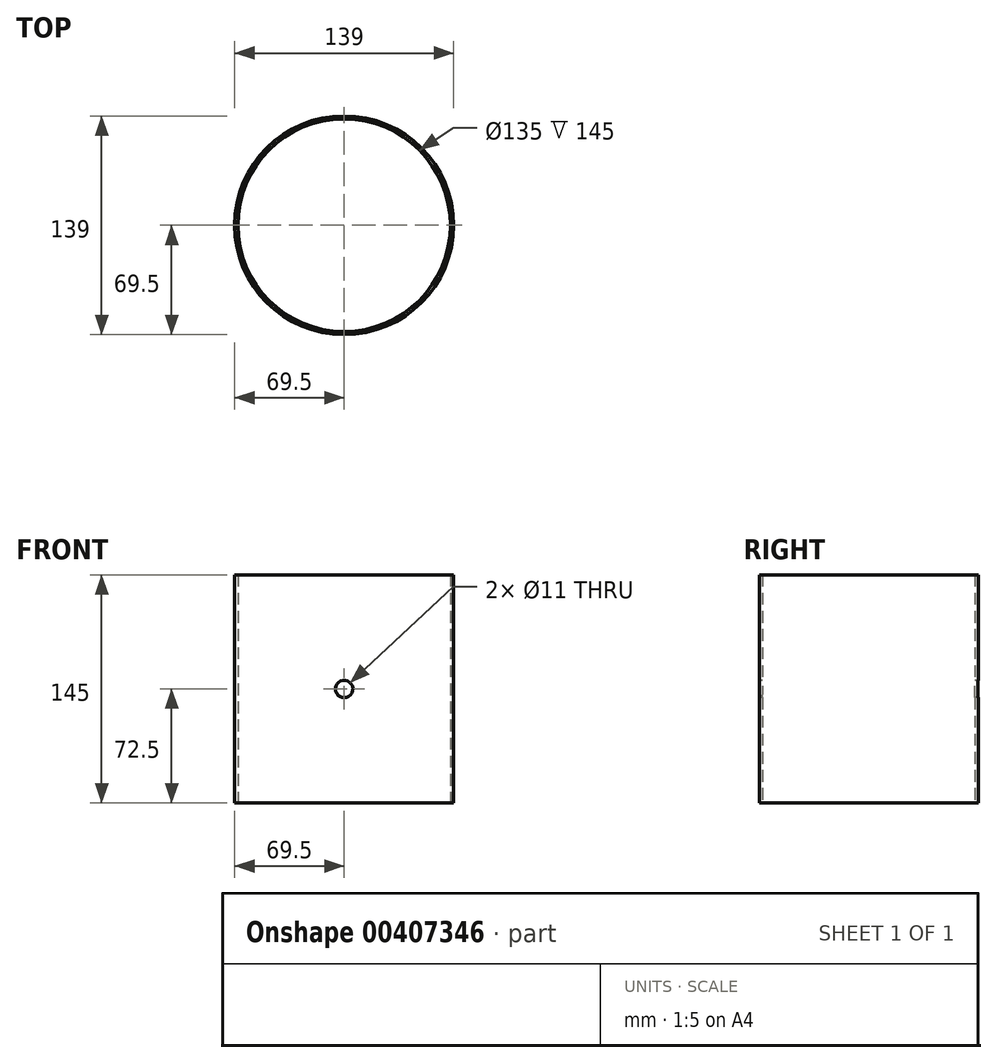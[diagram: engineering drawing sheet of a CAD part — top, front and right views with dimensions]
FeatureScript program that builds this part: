
annotation { "Feature Type Name" : "Feature", "Feature Type Description" : "" }
export const myFeature = defineFeature(function(context is Context, id is Id, definition is map)
    precondition{}
    {
        {
            var Q0;
            Q0=qCreatedBy(makeId("Top.planeOp"),FACE);
            var sketch = newSketch(context, id + "F0", { "sketchPlane" : qUnion([Q0])});
            skCircle(sketch, "E0", {"center": v(0, 0) * mm, "radius": 69.5 * mm});
            skCircle(sketch, "E1", {"center": v(0, 0) * mm, "radius": 67.5 * mm});
            skSolve(sketch);
        }
        {
            var Q0;
            Q0 = qSketchRegion(id + "F0", true);
            extrude(context, id + "F1", {"entities" : qUnion([Q0]), "depth" : 145 / 2 * mm, "hasSecondDirection" : true, "secondDirectionOppositeDirection" : true, "secondDirectionDepth" : (145 / 2) * mm});
        }
        {
            var Q0;
            Q0=qCreatedBy(makeId("Front.planeOp"),FACE);
            var sketch = newSketch(context, id + "F2", { "sketchPlane" : qUnion([Q0])});
            skCircle(sketch, "E2", {"center": v(0, 0) * mm, "radius": 5.5 * mm});
            skSolve(sketch);
        }
        {
            var Q0;
            Q0 = qSketchRegion(id + "F2", true);
            extrude(context, id + "F3", {"entities" : qUnion([Q0]), "operationType" : NewBodyOperationType.REMOVE, "oppositeDirection" : true, "depth" : 110 * mm, "hasSecondDirection" : true, "secondDirectionOppositeDirection" : false, "secondDirectionDepth" : 110 * mm});
        }
    });
